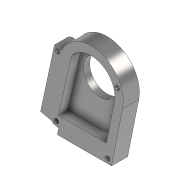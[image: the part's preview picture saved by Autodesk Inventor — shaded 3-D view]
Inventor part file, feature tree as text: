
AUTODESK INVENTOR PART (.ipt)
format: ipt  version: 2020.3 (Build 243373010, 373A)  size: 182,272 bytes
history: native  units: mm
features: sketch x3, extrude x2, projected_geometry x2, mirror x1, delete_face x1, fillet x1
ambient origin geometry x8: Origin, YZ Plane, XZ Plane, XY Plane, X Axis, Y Axis, Z Axis, Center Point
bodies: Solid3 (feature_tree)
feature tree (10):
  extrude  "Extrusion4"  Depth=10.0mm
  sketch  "Sketch5"  dims[d26=15.0mm d27=0.0mm d28=92.335mm d29=5.0mm]
  extrude  "Extrusion6"  Depth=5.0mm
  mirror  "Mirror1"
  delete_face  "Delete Face1"
  fillet  "Fillet2"  Radius=5.0mm
  sketch  "Sketch4"  dims[d21=10.0mm d22=0.0mm d23=34.0mm]
  projected_geometry  "Projected Loop1"
  sketch  "Sketch6"
  projected_geometry  "Projected Loop2"
